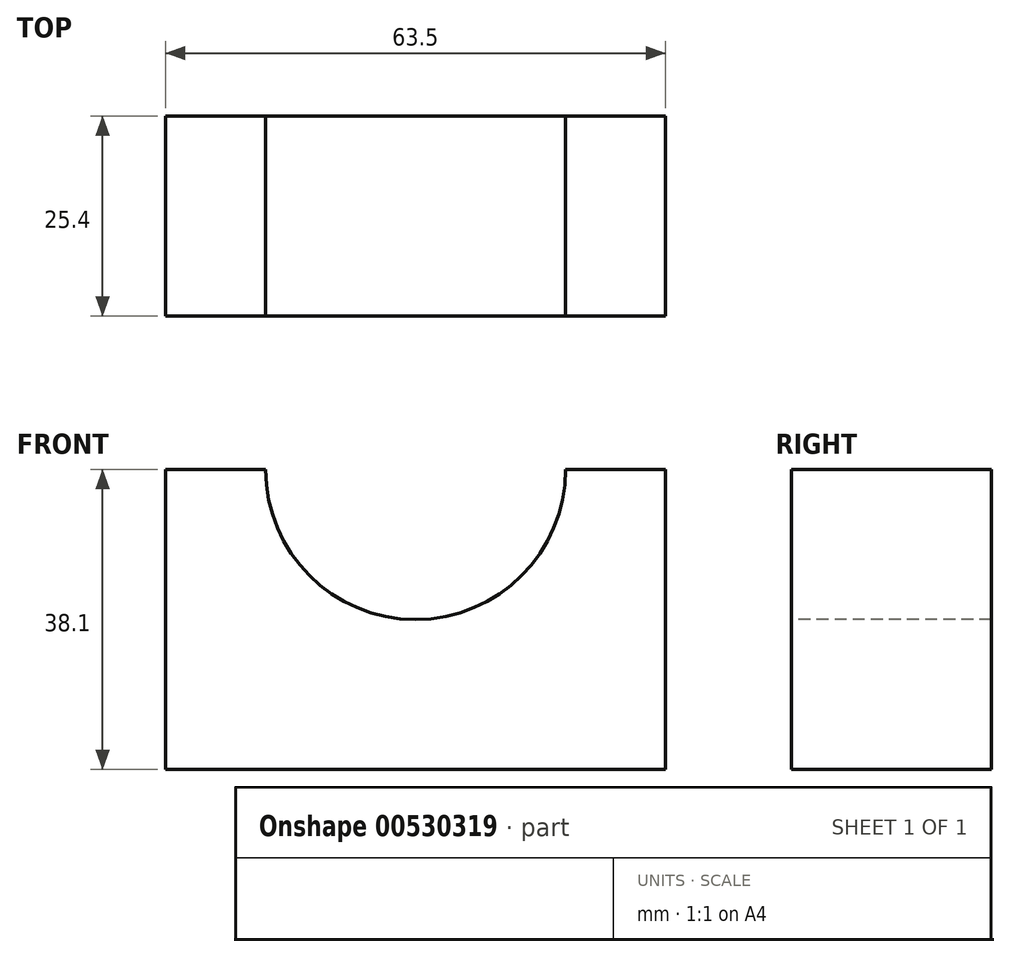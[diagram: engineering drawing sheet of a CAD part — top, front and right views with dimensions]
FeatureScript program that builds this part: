
annotation { "Feature Type Name" : "Feature", "Feature Type Description" : "" }
export const myFeature = defineFeature(function(context is Context, id is Id, definition is map)
    precondition{}
    {
        {
            var Q0;
            Q0=qCreatedBy(makeId("Front.planeOp"),FACE);
            var sketch = newSketch(context, id + "F0", { "sketchPlane" : qUnion([Q0])});
            skLineSegment(sketch, "E0.bottom", {"start": v(-70.69, 48.2) * mm, "end": v(-7.19, 48.2) * mm});
            skLineSegment(sketch, "E0.top", {"start": v(-70.69, 10.1) * mm, "end": v(-7.19, 10.1) * mm});
            skLineSegment(sketch, "E0.left", {"start": v(-70.69, 48.2) * mm, "end": v(-70.69, 10.1) * mm});
            skLineSegment(sketch, "E0.right", {"start": v(-7.19, 48.2) * mm, "end": v(-7.19, 10.1) * mm});
            skSolve(sketch);
        }
        {
            var Q0;
            Q0=makeQuery(id+"F0.imprint","IMPRINT",FACE,{"disambiguationData":[TD([[makeQuery(id+"F0.imprint","IMPRINT",EDGE,{"derivedFrom":sQuery(id+"F0.wireOp",EDGE,"E0.bottom")}),-1.0]])]});
            extrude(context, id + "F1", {"entities" : qUnion([Q0]), "depth" : 25.4 * mm, "offsetDistance" : 25.4 * mm});
        }
        {
            var Q0;
            Q0=makeQuery(id+"F1.opExtrude","CAP_FACE",FACE,{"disambiguationData":[OSD([sQuery(id+"F0.wireOp",EDGE,"E0.bottom"),sQuery(id+"F0.wireOp",EDGE,"E0.top"),sQuery(id+"F0.wireOp",EDGE,"E0.left"),sQuery(id+"F0.wireOp",EDGE,"E0.right")])],"isStart":false});
            var sketch = newSketch(context, id + "F2", { "sketchPlane" : qUnion([Q0])});
            skLineSegment(sketch, "E1", {"start": v(-70.69, 48.2) * mm, "end": v(-57.99, 48.2) * mm});
            skLineSegment(sketch, "E2", {"start": v(-7.19, 48.2) * mm, "end": v(-19.89, 48.2) * mm});
            skLineSegment(sketch, "E3", {"start": v(-70.69, 10.1) * mm, "end": v(-38.94, 10.1) * mm});
            skLineSegment(sketch, "E4", {"start": v(-38.94, 10.1) * mm, "end": v(-38.94, 29.15) * mm});
            skArc(sketch, "E5", {"start": v(-57.99, 48.2) * mm, "mid": v(-38.94, 29.15) * mm, "end": v(-19.89, 48.2) * mm});
            skSolve(sketch);
        }
        {
            var Q0;
            Q0 = qSketchRegion(id + "F2", true);
            var Q1;
            {var subQ0=sQuery(id+"F2.wireOp",EDGE,"E5");var subQ3=makeQuery(id+"F2.imprint","INTERSECT",VERTEX,{"derivedFrom":[sQuery(id+"F2.wireOp",EDGE,"E4"),subQ0]});Q1=makeQuery(id+"F2.imprint","IMPRINT",FACE,{"disambiguationData":[TD([[makeQuery(id+"F2.imprint","IMPRINT",EDGE,{"disambiguationData":[TD([[subQ3,1.0]])],"derivedFrom":subQ0}),1.0]])]});}
            extrude(context, id + "F3", {"entities" : qUnion([Q0, Q1]), "operationType" : NewBodyOperationType.REMOVE, "endBound" : BoundingType.THROUGH_ALL, "oppositeDirection" : true, "depth" : 25.4 * mm, "offsetDistance" : 25.4 * mm});
        }
    });
